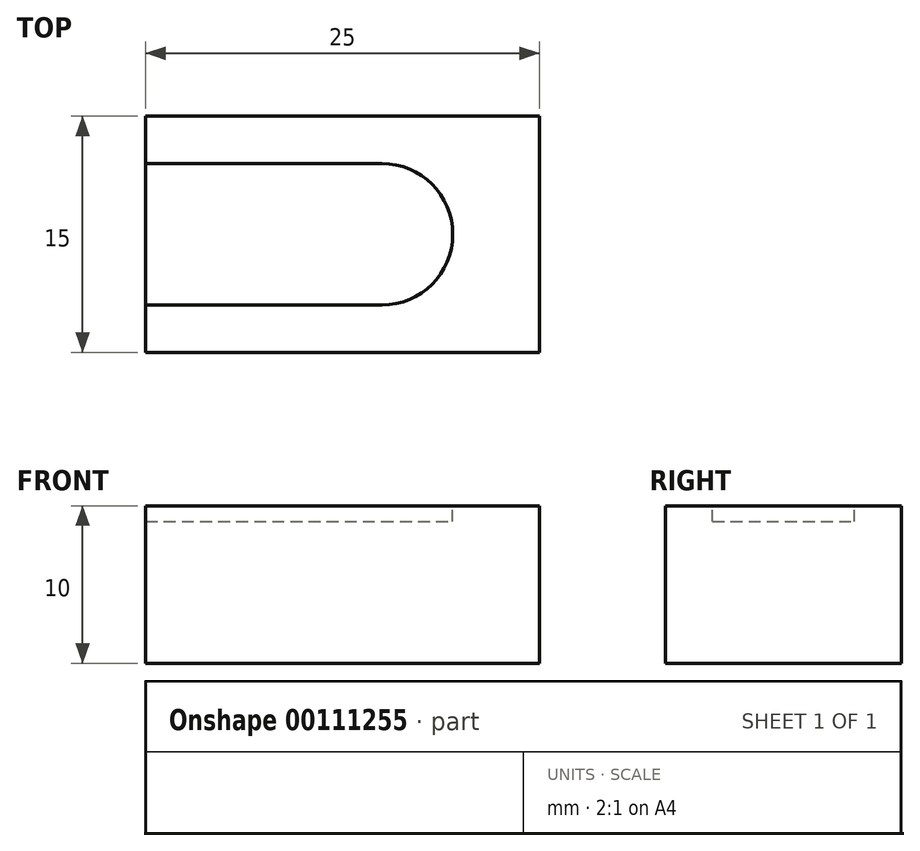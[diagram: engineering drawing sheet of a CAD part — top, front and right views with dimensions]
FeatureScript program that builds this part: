
annotation { "Feature Type Name" : "Feature", "Feature Type Description" : "" }
export const myFeature = defineFeature(function(context is Context, id is Id, definition is map)
    precondition{}
    {
        {
            var Q0;
            Q0=qCreatedBy(makeId("Front.planeOp"),FACE);
            var sketch = newSketch(context, id + "F0", { "sketchPlane" : qUnion([Q0])});
            skLineSegment(sketch, "E0.bottom", {"start": v(0, 0) * mm, "end": v(25, 0) * mm});
            skLineSegment(sketch, "E0.top", {"start": v(0, 10) * mm, "end": v(25, 10) * mm});
            skLineSegment(sketch, "E0.left", {"start": v(0, 0) * mm, "end": v(0, 10) * mm});
            skLineSegment(sketch, "E0.right", {"start": v(25, 0) * mm, "end": v(25, 10) * mm});
            skSolve(sketch);
        }
        {
            var Q0;
            Q0=makeQuery(id+"F0.imprint","IMPRINT",FACE,{"disambiguationData":[TD([[makeQuery(id+"F0.imprint","IMPRINT",EDGE,{"derivedFrom":sQuery(id+"F0.wireOp",EDGE,"E0.bottom")}),1.0]])]});
            extrude(context, id + "F1", {"entities" : qUnion([Q0]), "depth" : 15 * mm});
        }
        {
            var Q0;
            Q0=makeQuery(id+"F1.opExtrude","SWEPT_FACE",FACE,{"disambiguationData":[OSD([sQuery(id+"F0.wireOp",EDGE,"E0.top")])]});
            var sketch = newSketch(context, id + "F2", { "sketchPlane" : qUnion([Q0])});
            skLineSegment(sketch, "E1", {"start": v(0, -3) * mm, "end": v(15, -3) * mm});
            skLineSegment(sketch, "E2", {"start": v(0, -12) * mm, "end": v(15, -12) * mm});
            skArc(sketch, "E3", {"start": v(15, -12) * mm, "mid": v(19.5, -7.5) * mm, "end": v(15, -3) * mm});
            skSolve(sketch);
        }
        {
            var Q0;
            {var subQ0=sQuery(id+"F2.wireOp",EDGE,"E1");Q0=makeQuery(id+"F2.imprint","IMPRINT",FACE,{"disambiguationData":[TD([[makeQuery(id+"F2.imprint","IMPRINT",EDGE,{"derivedFrom":subQ0}),-1.0]])]});}
            extrude(context, id + "F3", {"entities" : qUnion([Q0]), "operationType" : NewBodyOperationType.REMOVE, "oppositeDirection" : true, "depth" : 1 * mm});
        }
    });
